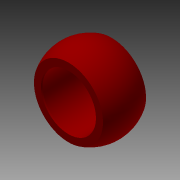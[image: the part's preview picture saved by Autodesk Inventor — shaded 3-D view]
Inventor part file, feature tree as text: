
AUTODESK INVENTOR PART (.ipt)
format: ipt  version: 2016 SP1 (Build 200210100, 210)  size: 114,176 bytes
history: native  units: mm (DEFAULTED — no unit token found)
features: sketch x2, revolve x1, extrude x1, hole x1, chamfer x1
ambient origin geometry x8: Origin, YZ Plane, XZ Plane, XY Plane, X Axis, Y Axis, Z Axis, Center Point
bodies: Solid1 (feature_tree)
feature tree (6):
  revolve  "Revolution1"  Angle=90.0deg
  extrude  "Extrusion3"  Depth=6.35mm TaperAngle=0.0deg
  hole  "Hole1"  [1 undecoded]
  chamfer  "Chamfer1"  Distance=0.3048mm Angle=30.0deg
  sketch  "Sketch1"  dims[d0=24.003mm d1=90.0deg]
  sketch  "Sketch4"  dims[d8=12.7mm d9=25.4mm d10=0.0mm d11=25.4mm d12=25.4mm d13=15.875mm d14=12.7mm d15=9.525mm d16=6.35mm d17=14.3117mm d18=19.05mm d19=20.594885mm d20=0.3048mm d21=3.175mm d22=30.0deg]
note: 1 required parameter value undecoded (feature->parameter linkage not recoverable at this tier; creation-order binding heuristic only, values carry confidence <= 0.55)
